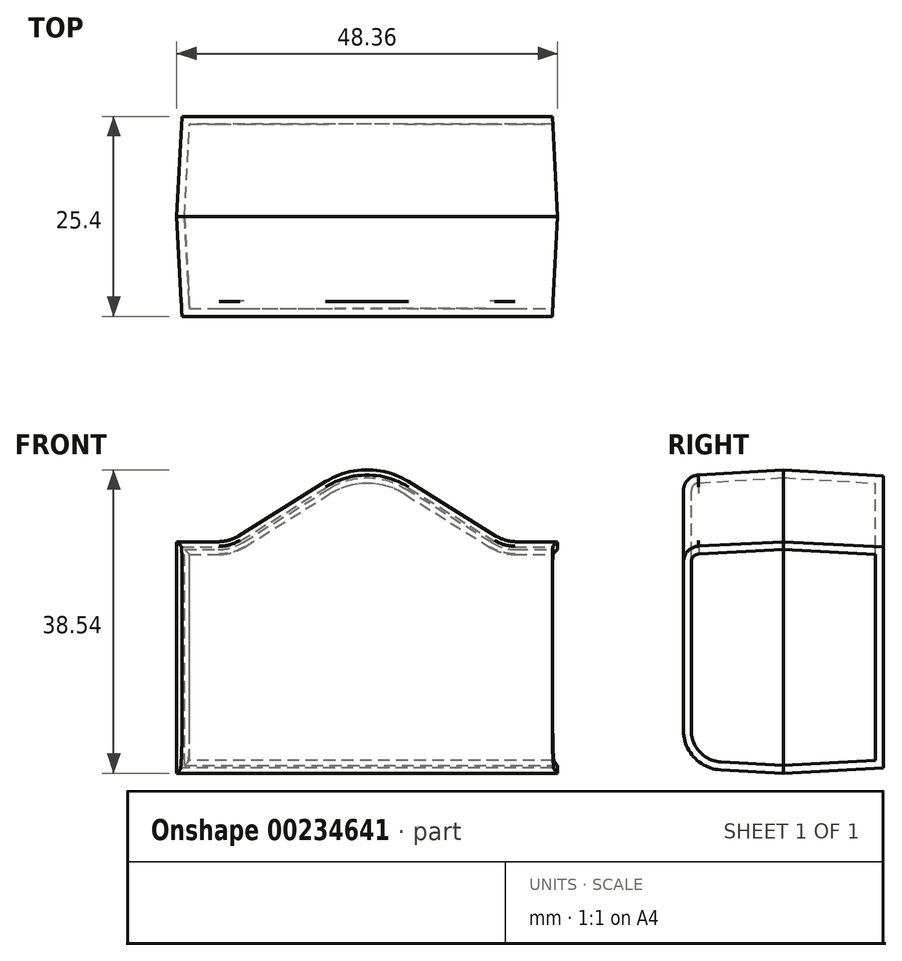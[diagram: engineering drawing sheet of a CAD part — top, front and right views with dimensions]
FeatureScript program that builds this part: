
annotation { "Feature Type Name" : "Feature", "Feature Type Description" : "" }
export const myFeature = defineFeature(function(context is Context, id is Id, definition is map)
    precondition{}
    {
        {
            var Q0;
            Q0=qCreatedBy(makeId("Front.planeOp"),FACE);
            var sketch = newSketch(context, id + "F0", { "sketchPlane" : qUnion([Q0])});
            skLineSegment(sketch, "E0", {"start": v(0, 0) * mm, "end": v(0, 43.72) * mm, "construction": true});
            skLineSegment(sketch, "E1.bottom", {"start": v(-24.18, 0) * mm, "end": v(24.18, 0) * mm});
            skLineSegment(sketch, "E1.top", {"start": v(-24.18, 29.4) * mm, "end": v(-17.53, 29.4) * mm});
            skLineSegment(sketch, "E1.left", {"start": v(-24.18, 0) * mm, "end": v(-24.18, 29.4) * mm});
            skLineSegment(sketch, "E1.right", {"start": v(24.18, 0) * mm, "end": v(24.18, 29.4) * mm});
            skLineSegment(sketch, "E2", {"start": v(-17.53, 29.4) * mm, "end": v(0, 40.32) * mm});
            skLineSegment(sketch, "E3.MirrorCS", {"start": v(17.53, 29.4) * mm, "end": v(0, 40.32) * mm});
            skLineSegment(sketch, "E4.trimOffspring", {"start": v(17.53, 29.4) * mm, "end": v(24.18, 29.4) * mm});
            skSolve(sketch);
        }
        {
            var Q0;
            Q0 = qSketchRegion(id + "F0", true);
            extrude(context, id + "F1", {"entities" : qUnion([Q0]), "endBound" : BoundingType.SYMMETRIC, "depth" : 25.4 * mm, "hasDraft" : true, "draftAngle" : 3 * degree, "draftPullDirection" : true});
        }
        {
            var Q0;
            Q0=makeQuery(id+"F1.opExtrude","CAP_EDGE",EDGE,{"disambiguationData":[OSD([sQuery(id+"F0.wireOp",EDGE,"E1.bottom")])],"isStart":false});
            fillet(context, id + "F2", {"entities" : qUnion([Q0]), "radius" : 5 * mm, "tangentPropagation" : true, "allowEdgeOverflow" : false});
        }
        {
            var Q0;
            Q0=makeQuery(id+"F1.*.split.splitOp","SPLIT",EDGE,{"derivedFrom":makeQuery(id+"F1.opExtrude","SWEPT_EDGE",EDGE,{"disambiguationData":[OSD([sQuery(id+"F0.wireOp",EDGE,"E3.MirrorCS"),sQuery(id+"F0.wireOp",EDGE,"E4.trimOffspring")])]})});
            var Q1;
            Q1=makeQuery(id+"F1.*.split.splitOp","SPLIT",EDGE,{"derivedFrom":makeQuery(id+"F1.opExtrude","SWEPT_EDGE",EDGE,{"disambiguationData":[OSD([sQuery(id+"F0.wireOp",EDGE,"E3.MirrorCS"),sQuery(id+"F0.wireOp",EDGE,"E4.trimOffspring")])]}),"isFromBackBody":true});
            var Q2;
            Q2=makeQuery(id+"F1.*.split.splitOp","SPLIT",EDGE,{"derivedFrom":makeQuery(id+"F1.opExtrude","SWEPT_EDGE",EDGE,{"disambiguationData":[OSD([sQuery(id+"F0.wireOp",EDGE,"E1.top"),sQuery(id+"F0.wireOp",EDGE,"E2")])]}),"isFromBackBody":true});
            var Q3;
            Q3=makeQuery(id+"F1.*.split.splitOp","SPLIT",EDGE,{"derivedFrom":makeQuery(id+"F1.opExtrude","SWEPT_EDGE",EDGE,{"disambiguationData":[OSD([sQuery(id+"F0.wireOp",EDGE,"E1.top"),sQuery(id+"F0.wireOp",EDGE,"E2")])]})});
            fillet(context, id + "F3", {"entities" : qUnion([Q0, Q1, Q2, Q3]), "radius" : 5 * mm, "tangentPropagation" : true, "allowEdgeOverflow" : false});
        }
        {
            var Q0;
            Q0=makeQuery(id+"F1.*.split.splitOp","SPLIT",EDGE,{"derivedFrom":makeQuery(id+"F1.opExtrude","SWEPT_EDGE",EDGE,{"disambiguationData":[OSD([sQuery(id+"F0.wireOp",EDGE,"E2"),sQuery(id+"F0.wireOp",EDGE,"E3.MirrorCS")])]})});
            var Q1;
            Q1=makeQuery(id+"F1.*.split.splitOp","SPLIT",EDGE,{"derivedFrom":makeQuery(id+"F1.opExtrude","SWEPT_EDGE",EDGE,{"disambiguationData":[OSD([sQuery(id+"F0.wireOp",EDGE,"E2"),sQuery(id+"F0.wireOp",EDGE,"E3.MirrorCS")])]}),"isFromBackBody":true});
            fillet(context, id + "F4", {"entities" : qUnion([Q0, Q1]), "radius" : 10 * mm, "tangentPropagation" : true, "allowEdgeOverflow" : false});
        }
        {
            var Q0;
            Q0=makeQuery(id+"F1.opExtrude","CAP_EDGE",EDGE,{"disambiguationData":[OSD([sQuery(id+"F0.wireOp",EDGE,"E2")])],"isStart":false});
            fillet(context, id + "F5", {"entities" : qUnion([Q0]), "radius" : 2 * mm, "tangentPropagation" : true, "allowEdgeOverflow" : false});
        }
        {
            var Q0;
            Q0=makeQuery(id+"F1.*.split.splitOp","SPLIT",FACE,{"derivedFrom":makeQuery(id+"F1.opExtrude","SWEPT_FACE",FACE,{"disambiguationData":[OSD([sQuery(id+"F0.wireOp",EDGE,"E1.right")])]})});
            var Q1;
            Q1=makeQuery(id+"F1.*.split.splitOp","SPLIT",FACE,{"derivedFrom":makeQuery(id+"F1.opExtrude","SWEPT_FACE",FACE,{"disambiguationData":[OSD([sQuery(id+"F0.wireOp",EDGE,"E1.right")])]}),"isFromBackBody":true});
            shell(context, id + "F6", {"entities" : qUnion([Q0, Q1]), "thickness" : 1 * mm});
        }
    });
